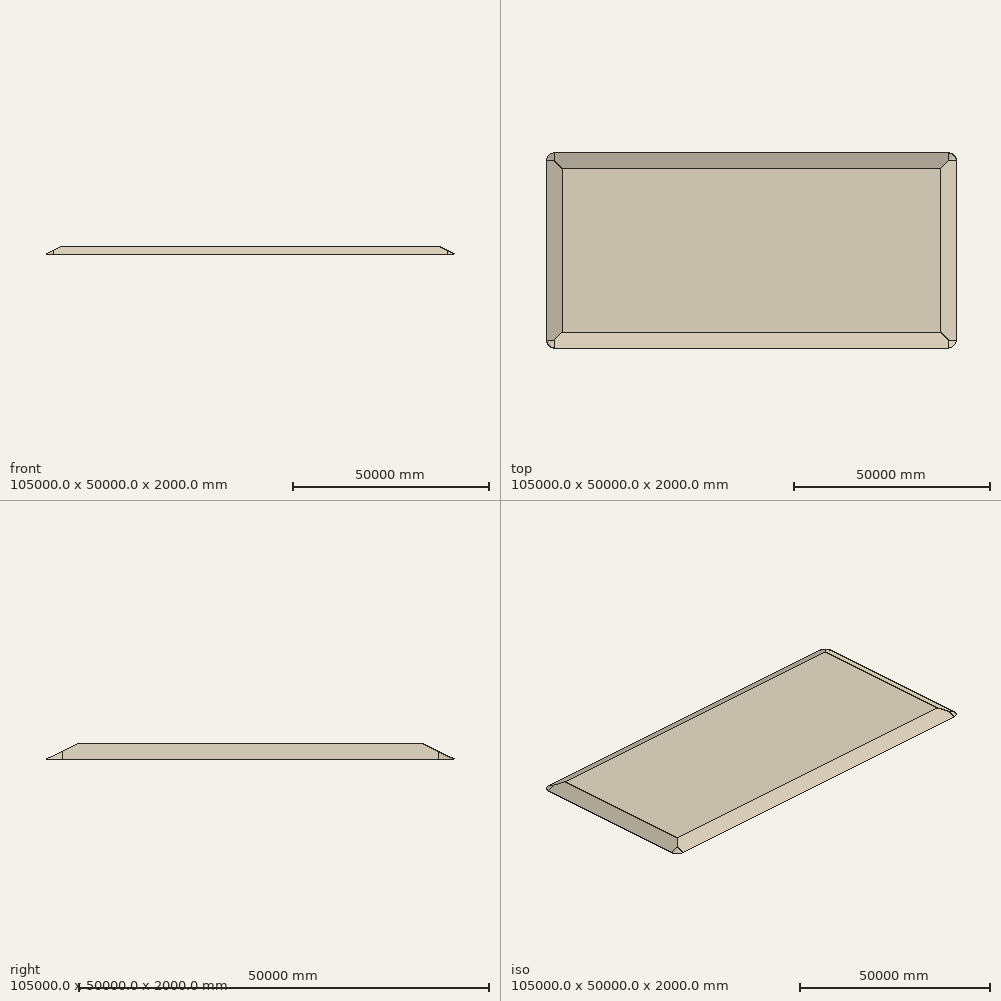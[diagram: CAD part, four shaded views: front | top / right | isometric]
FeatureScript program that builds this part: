
annotation { "Feature Type Name" : "Feature", "Feature Type Description" : "" }
export const myFeature = defineFeature(function(context is Context, id is Id, definition is map)
    precondition{}
    {
        {
            var Q0;
            Q0=qCreatedBy(makeId("Top.planeOp"),FACE);
            var sketch = newSketch(context, id + "F0", { "sketchPlane" : qUnion([Q0])});
            skLineSegment(sketch, "E0.bottom", {"start": v(-102898.3, 52005.58) * mm, "end": v(-1998.3, 52005.58) * mm});
            skLineSegment(sketch, "E0.top", {"start": v(-102898.3, 2005.58) * mm, "end": v(-1998.3, 2005.58) * mm});
            skLineSegment(sketch, "E0.left", {"start": v(-104948.3, 49955.58) * mm, "end": v(-104948.3, 4055.58) * mm});
            skLineSegment(sketch, "E0.right", {"start": v(51.7, 49955.58) * mm, "end": v(51.7, 4055.58) * mm});
            skPoint(sketch, "E1.visualSharp", {"position": v(-104948.3, 52005.58) * mm});
            skArc(sketch, "E1.filletArc", {"start": v(-102898.3, 52005.58) * mm, "mid": v(-104347.86, 51405.15) * mm, "end": v(-104948.3, 49955.58) * mm});
            skPoint(sketch, "E2.visualSharp", {"position": v(-104948.3, 2005.58) * mm});
            skArc(sketch, "E2.filletArc", {"start": v(-104948.3, 4055.58) * mm, "mid": v(-104347.86, 2606.01) * mm, "end": v(-102898.3, 2005.58) * mm});
            skPoint(sketch, "E3.visualSharp", {"position": v(51.7, 2005.58) * mm});
            skArc(sketch, "E3.filletArc", {"start": v(-1998.3, 2005.58) * mm, "mid": v(-548.72, 2606.01) * mm, "end": v(51.7, 4055.58) * mm});
            skPoint(sketch, "E4.visualSharp", {"position": v(51.7, 52005.58) * mm});
            skArc(sketch, "E4.filletArc", {"start": v(51.7, 49955.58) * mm, "mid": v(-548.72, 51405.15) * mm, "end": v(-1998.3, 52005.58) * mm});
            skSolve(sketch);
        }
        {
            var Q0;
            Q0=makeQuery(id+"F0.imprint","IMPRINT",FACE,{"disambiguationData":[TD([[makeQuery(id+"F0.imprint","IMPRINT",EDGE,{"derivedFrom":sQuery(id+"F0.wireOp",EDGE,"E0.bottom")}),-1.0]])]});
            extrude(context, id + "F1", {"entities" : qUnion([Q0]), "depth" : 2000 * mm, "hasDraft" : true, "draftAngle" : 64 * degree, "draftPullDirection" : true});
        }
    });
